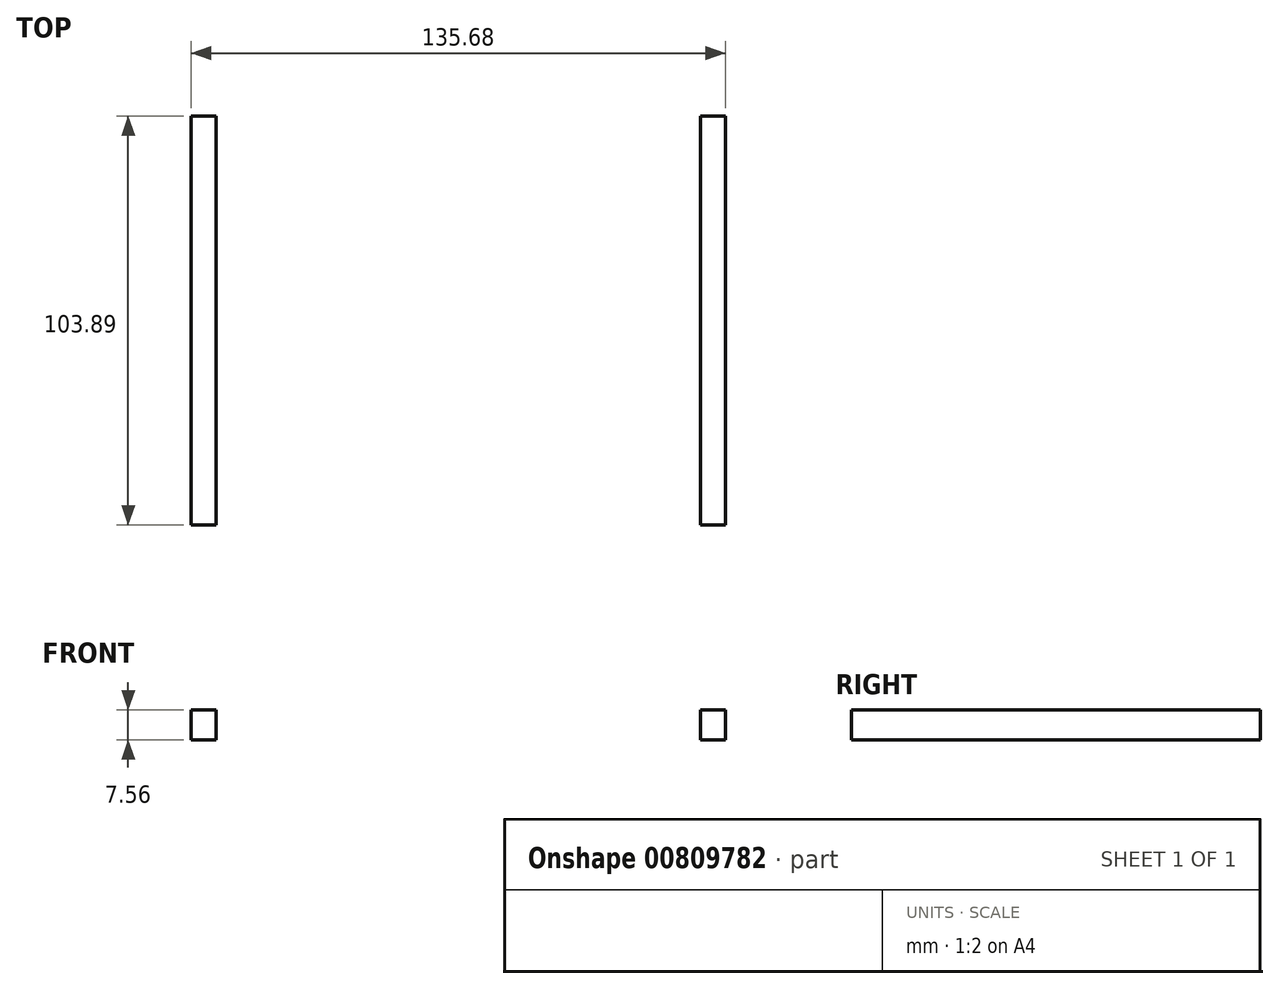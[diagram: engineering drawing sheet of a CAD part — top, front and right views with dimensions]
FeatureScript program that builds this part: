
annotation { "Feature Type Name" : "Feature", "Feature Type Description" : "" }
export const myFeature = defineFeature(function(context is Context, id is Id, definition is map)
    precondition{}
    {
        {
            var Q0;
            Q0=qCreatedBy(makeId("Front.planeOp"),FACE);
            var sketch = newSketch(context, id + "F0", { "sketchPlane" : qUnion([Q0])});
            skLineSegment(sketch, "E0.bottom", {"start": v(-67.84, 26.58) * mm, "end": v(-61.47, 26.58) * mm});
            skLineSegment(sketch, "E0.top", {"start": v(-67.84, 19.02) * mm, "end": v(-61.47, 19.02) * mm});
            skLineSegment(sketch, "E0.left", {"start": v(-67.84, 26.58) * mm, "end": v(-67.84, 19.02) * mm});
            skLineSegment(sketch, "E0.right", {"start": v(-61.47, 26.58) * mm, "end": v(-61.47, 19.02) * mm});
            skSolve(sketch);
        }
        {
            var Q0;
            Q0 = qSketchRegion(id + "F0", true);
            extrude(context, id + "F1", {"entities" : qUnion([Q0]), "depth" : 103.89 * mm, "offsetDistance" : 25.4 * mm});
        }
        {
            var Q0;
            Q0=makeQuery(id+"F1.opExtrude","SWEPT_BODY",BODY,{"disambiguationData":[OSD([sQuery(id+"F0.wireOp",EDGE,"E0.bottom"),sQuery(id+"F0.wireOp",EDGE,"E0.top"),sQuery(id+"F0.wireOp",EDGE,"E0.left"),sQuery(id+"F0.wireOp",EDGE,"E0.right")])]});
            var Q1;
            Q1=qCreatedBy(makeId("Right.planeOp"),FACE);
            mirror(context, id + "F2", {"entities" : qUnion([Q0]), "mirrorPlane" : qUnion([Q1])});
        }
    });
